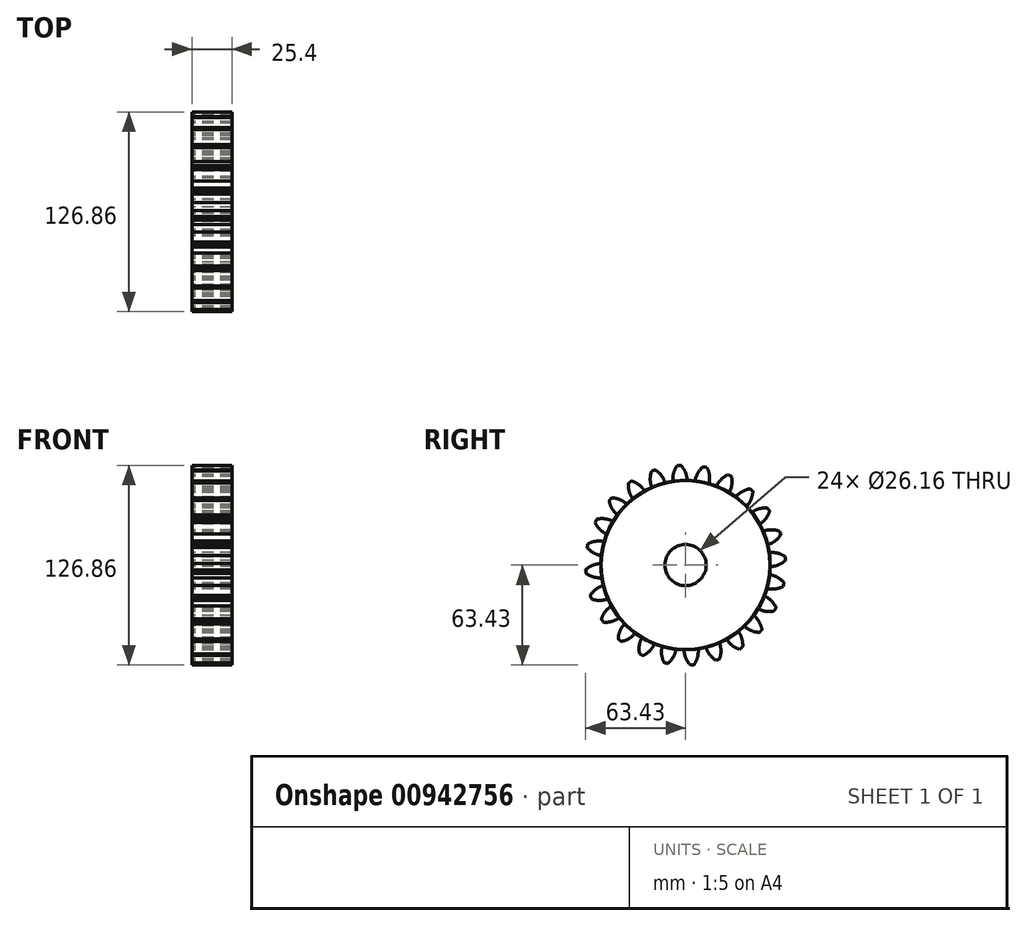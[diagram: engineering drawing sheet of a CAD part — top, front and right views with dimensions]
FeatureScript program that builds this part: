
annotation { "Feature Type Name" : "Feature", "Feature Type Description" : "" }
export const myFeature = defineFeature(function(context is Context, id is Id, definition is map)
    precondition{}
    {
        {
            var Q0;
            Q0=qCreatedBy(makeId("Right.planeOp"),FACE);
            var sketch = newSketch(context, id + "F0", { "sketchPlane" : qUnion([Q0])});
            skCircle(sketch, "E0", {"center": v(0, 0) * mm, "radius": 63.5 * mm, "construction": true});
            skCircle(sketch, "E1", {"center": v(0, 0) * mm, "radius": 58.67 * mm});
            skCircle(sketch, "E2", {"center": v(0, 0) * mm, "radius": 53.72 * mm});
            skLineSegment(sketch, "E3", {"start": v(0, 0) * mm, "end": v(0, 112.5) * mm, "construction": true});
            skLineSegment(sketch, "E4", {"start": v(0, 0) * mm, "end": v(-7.37, 112.5) * mm, "construction": true});
            skLineSegment(sketch, "E5", {"start": v(0, 58.67) * mm, "end": v(-122.15, 58.67) * mm, "construction": true});
            skLineSegment(sketch, "E6", {"start": v(0, 58.67) * mm, "end": v(-122.15, 14.21) * mm, "construction": true});
            skCircle(sketch, "E7", {"center": v(0, 0) * mm, "radius": 55.14 * mm, "construction": true});
            skCircle(sketch, "E8", {"center": v(0, 58.67) * mm, "radius": 14.6 * mm, "construction": true});
            skCircle(sketch, "E9", {"center": v(-13.63, 53.42) * mm, "radius": 14.6 * mm, "construction": true});
            skArc(sketch, "E10", {"start": v(0, 58.67) * mm, "mid": v(-1.26, 61.2) * mm, "end": v(-2.99, 63.43) * mm});
            skArc(sketch, "E11", {"start": v(0.97, 53.71) * mm, "mid": v(0.7, 56.24) * mm, "end": v(0, 58.67) * mm});
            skArc(sketch, "E12.MirrorCS", {"start": v(-7.66, 58.17) * mm, "mid": v(-6.74, 60.84) * mm, "end": v(-5.32, 63.28) * mm});
            skArc(sketch, "E13.MirrorCS", {"start": v(-7.98, 53.13) * mm, "mid": v(-8.04, 55.66) * mm, "end": v(-7.66, 58.17) * mm});
            skArc(sketch, "E14", {"start": v(-5.32, 63.28) * mm, "mid": v(-4.15, 63.32) * mm, "end": v(-2.99, 63.43) * mm});
            skCircle(sketch, "E15", {"center": v(0, 0) * mm, "radius": 13.08 * mm});
            skSolve(sketch);
        }
        {
            var Q0;
            {var subQ0=sQuery(id+"F0.wireOp",EDGE,"E2");var subQ1=makeQuery(id+"F0.imprint","INTERSECT",VERTEX,{"derivedFrom":[subQ0,sQuery(id+"F0.wireOp",EDGE,"E11")]});Q0=makeQuery(id+"F0.imprint","IMPRINT",FACE,{"disambiguationData":[TD([[makeQuery(id+"F0.imprint","IMPRINT",EDGE,{"disambiguationData":[TD([[subQ1,-1.0]])],"derivedFrom":subQ0}),1.0]])]});}
            var Q1;
            {var subQ0=sQuery(id+"F0.wireOp",EDGE,"E10");Q1=makeQuery(id+"F0.imprint","IMPRINT",FACE,{"disambiguationData":[TD([[makeQuery(id+"F0.imprint","IMPRINT",EDGE,{"derivedFrom":subQ0}),1.0]])]});}
            var Q2;
            {var subQ0=sQuery(id+"F0.wireOp",EDGE,"E11");Q2=makeQuery(id+"F0.imprint","IMPRINT",FACE,{"disambiguationData":[TD([[makeQuery(id+"F0.imprint","IMPRINT",EDGE,{"derivedFrom":subQ0}),1.0]])]});}
            extrude(context, id + "F1", {"entities" : qUnion([Q0, Q1, Q2]), "depth" : 25.4 * mm, "offsetDistance" : 25.4 * mm});
        }
        {
            var Q0;
            Q0=makeQuery(id+"F1.opExtrude","SWEPT_BODY",BODY,{"disambiguationData":[OSD([sQuery(id+"F0.wireOp",EDGE,"E2"),sQuery(id+"F0.wireOp",EDGE,"E10"),sQuery(id+"F0.wireOp",EDGE,"E11"),sQuery(id+"F0.wireOp",EDGE,"E12.MirrorCS"),sQuery(id+"F0.wireOp",EDGE,"E13.MirrorCS"),sQuery(id+"F0.wireOp",EDGE,"E14")])]});
            var Q1;
            Q1=makeQuery(id+"F1.opExtrude","SWEPT_FACE",FACE,{"disambiguationData":[OSD([sQuery(id+"F0.wireOp",EDGE,"E2")])]});
            circularPattern(context, id + "F2", {"entities" : qUnion([Q0]), "axis" : qUnion([Q1]), "angle" : 15 * degree, "instanceCount" : 24});
        }
    });
